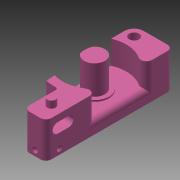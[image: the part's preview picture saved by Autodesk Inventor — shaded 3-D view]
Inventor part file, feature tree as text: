
AUTODESK INVENTOR PART (.ipt)
format: ipt  version: 2014 (Build 180170000, 170)  size: 137,728 bytes
history: native  units: mm
features: other x3, extrude x1, sketch x1, projected_geometry x1
ambient origin geometry x8: Origin, YZ Plane, XZ Plane, XY Plane, X Axis, Y Axis, Z Axis, Center Point
bodies: Solid1 (feature_tree)
feature tree (6):
  other  "bowden-extruder.ipt"
  extrude  "Extrusion1"  Depth=10.0mm TaperAngle=0.0deg
  other  "tensioner bottom::bowden-extruder.ipt"
  other  "TaggingFeature1"
  sketch  "Sketch1"  dims[d0=10.0mm d1=10.0mm d2=0.0mm]
  projected_geometry  "Projected Loop1"
